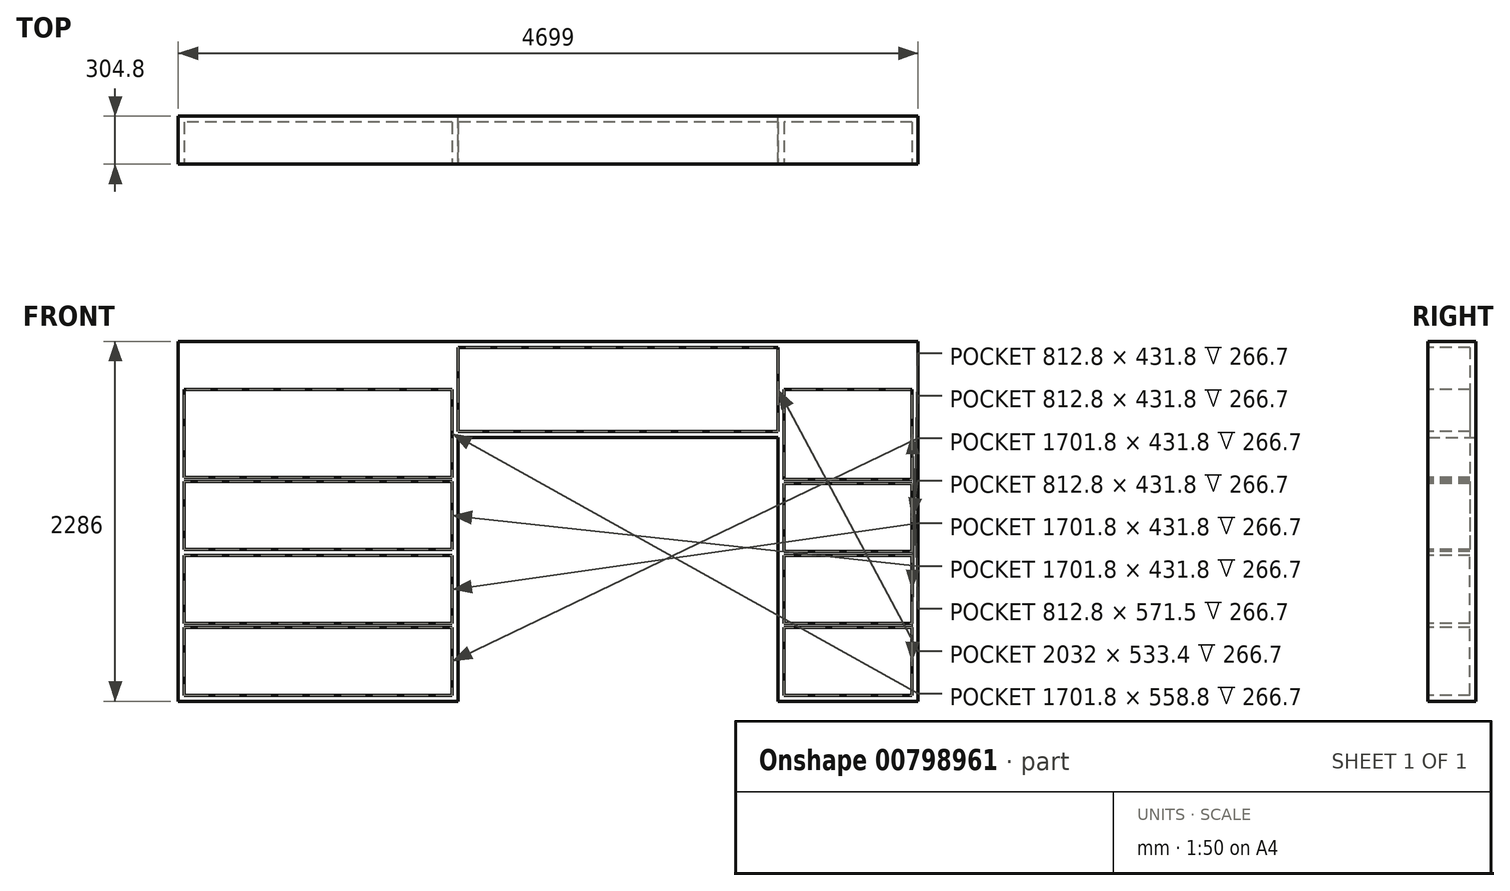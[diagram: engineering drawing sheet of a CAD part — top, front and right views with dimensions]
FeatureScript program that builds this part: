
annotation { "Feature Type Name" : "Feature", "Feature Type Description" : "" }
export const myFeature = defineFeature(function(context is Context, id is Id, definition is map)
    precondition{}
    {
        {
            var Q0;
            Q0=qCreatedBy(makeId("Front.planeOp"),FACE);
            var sketch = newSketch(context, id + "F0", { "sketchPlane" : qUnion([Q0])});
            skLineSegment(sketch, "E0", {"start": v(0, 0) * mm, "end": v(4699, 0) * mm});
            skLineSegment(sketch, "E1", {"start": v(4699, 0) * mm, "end": v(4699, 2286) * mm});
            skLineSegment(sketch, "E2", {"start": v(4699, 2286) * mm, "end": v(0, 2286) * mm});
            skLineSegment(sketch, "E3", {"start": v(0, 2286) * mm, "end": v(0, 0) * mm});
            skSolve(sketch);
        }
        {
            var Q0;
            Q0 = qSketchRegion(id + "F0", true);
            extrude(context, id + "F1", {"entities" : qUnion([Q0]), "depth" : 304.8 * mm, "offsetDistance" : 25.4 * mm});
        }
        {
            var Q0;
            Q0=qCreatedBy(makeId("Front.planeOp"),FACE);
            var sketch = newSketch(context, id + "F2", { "sketchPlane" : qUnion([Q0])});
            skLineSegment(sketch, "E4", {"start": v(1778, 0) * mm, "end": v(1778, 1676.4) * mm});
            skLineSegment(sketch, "E5", {"start": v(1778, 1676.4) * mm, "end": v(3810, 1676.4) * mm});
            skLineSegment(sketch, "E6", {"start": v(3810, 1676.4) * mm, "end": v(3810, 0) * mm});
            skLineSegment(sketch, "E7", {"start": v(3810, 0) * mm, "end": v(1778, 0) * mm});
            skSolve(sketch);
        }
        {
            var Q0;
            Q0 = qSketchRegion(id + "F2", true);
            extrude(context, id + "F3", {"entities" : qUnion([Q0]), "operationType" : NewBodyOperationType.REMOVE, "depth" : 304.8 * mm, "offsetDistance" : 25.4 * mm});
        }
        {
            var Q0;
            Q0=makeQuery(id+"F1.opExtrude","CAP_FACE",FACE,{"disambiguationData":[OSD([sQuery(id+"F0.wireOp",EDGE,"E0"),sQuery(id+"F0.wireOp",EDGE,"E1"),sQuery(id+"F0.wireOp",EDGE,"E2"),sQuery(id+"F0.wireOp",EDGE,"E3")])],"isStart":false});
            var sketch = newSketch(context, id + "F4", { "sketchPlane" : qUnion([Q0])});
            skLineSegment(sketch, "E8", {"start": v(3848.1, 38.1) * mm, "end": v(3848.1, 469.9) * mm});
            skLineSegment(sketch, "E9", {"start": v(3848.1, 469.9) * mm, "end": v(4660.9, 469.9) * mm});
            skLineSegment(sketch, "E10", {"start": v(4660.9, 469.9) * mm, "end": v(4660.9, 38.1) * mm});
            skLineSegment(sketch, "E11", {"start": v(4660.9, 38.1) * mm, "end": v(3848.1, 38.1) * mm});
            skSolve(sketch);
        }
        {
            var Q0;
            Q0 = qSketchRegion(id + "F4", true);
            extrude(context, id + "F5", {"entities" : qUnion([Q0]), "operationType" : NewBodyOperationType.REMOVE, "oppositeDirection" : true, "depth" : 266.7 * mm, "offsetDistance" : 25.4 * mm});
        }
        {
            var Q0;
            Q0=makeQuery(id+"F1.opExtrude","CAP_FACE",FACE,{"disambiguationData":[OSD([sQuery(id+"F0.wireOp",EDGE,"E0"),sQuery(id+"F0.wireOp",EDGE,"E1"),sQuery(id+"F0.wireOp",EDGE,"E2"),sQuery(id+"F0.wireOp",EDGE,"E3")])],"isStart":false});
            var sketch = newSketch(context, id + "F6", { "sketchPlane" : qUnion([Q0])});
            skLineSegment(sketch, "E12", {"start": v(3848.1, 927.1) * mm, "end": v(4660.9, 927.1) * mm});
            skLineSegment(sketch, "E13", {"start": v(4660.9, 927.1) * mm, "end": v(4660.9, 495.3) * mm});
            skLineSegment(sketch, "E14", {"start": v(4660.9, 495.3) * mm, "end": v(3848.1, 495.3) * mm});
            skLineSegment(sketch, "E15", {"start": v(3848.1, 495.3) * mm, "end": v(3848.1, 927.1) * mm});
            skSolve(sketch);
        }
        {
            var Q0;
            Q0 = qSketchRegion(id + "F6", true);
            extrude(context, id + "F7", {"entities" : qUnion([Q0]), "operationType" : NewBodyOperationType.REMOVE, "oppositeDirection" : true, "depth" : 266.7 * mm, "offsetDistance" : 25.4 * mm});
        }
        {
            var Q0;
            Q0=makeQuery(id+"F1.opExtrude","CAP_FACE",FACE,{"disambiguationData":[OSD([sQuery(id+"F0.wireOp",EDGE,"E0"),sQuery(id+"F0.wireOp",EDGE,"E1"),sQuery(id+"F0.wireOp",EDGE,"E2"),sQuery(id+"F0.wireOp",EDGE,"E3")])],"isStart":false});
            var sketch = newSketch(context, id + "F8", { "sketchPlane" : qUnion([Q0])});
            skLineSegment(sketch, "E16", {"start": v(38.1, 469.9) * mm, "end": v(38.1, 38.1) * mm});
            skLineSegment(sketch, "E17", {"start": v(38.1, 38.1) * mm, "end": v(1739.9, 38.1) * mm});
            skLineSegment(sketch, "E18", {"start": v(1739.9, 38.1) * mm, "end": v(1739.9, 469.9) * mm});
            skLineSegment(sketch, "E19", {"start": v(1739.9, 469.9) * mm, "end": v(38.1, 469.9) * mm});
            skSolve(sketch);
        }
        {
            var Q0;
            Q0 = qSketchRegion(id + "F8", true);
            extrude(context, id + "F9", {"entities" : qUnion([Q0]), "operationType" : NewBodyOperationType.REMOVE, "oppositeDirection" : true, "depth" : 266.7 * mm, "offsetDistance" : 25.4 * mm});
        }
        {
            var Q0;
            Q0=makeQuery(id+"F1.opExtrude","CAP_FACE",FACE,{"disambiguationData":[OSD([sQuery(id+"F0.wireOp",EDGE,"E0"),sQuery(id+"F0.wireOp",EDGE,"E1"),sQuery(id+"F0.wireOp",EDGE,"E2"),sQuery(id+"F0.wireOp",EDGE,"E3")])],"isStart":false});
            var sketch = newSketch(context, id + "F10", { "sketchPlane" : qUnion([Q0])});
            skLineSegment(sketch, "E20", {"start": v(3848.1, 1384.3) * mm, "end": v(3848.1, 952.5) * mm});
            skLineSegment(sketch, "E21", {"start": v(3848.1, 952.5) * mm, "end": v(4660.9, 952.5) * mm});
            skLineSegment(sketch, "E22", {"start": v(4660.9, 952.5) * mm, "end": v(4660.9, 1384.3) * mm});
            skLineSegment(sketch, "E23", {"start": v(4660.9, 1384.3) * mm, "end": v(3848.1, 1384.3) * mm});
            skSolve(sketch);
        }
        {
            var Q0;
            Q0 = qSketchRegion(id + "F10", true);
            extrude(context, id + "F11", {"entities" : qUnion([Q0]), "operationType" : NewBodyOperationType.REMOVE, "oppositeDirection" : true, "depth" : 266.7 * mm, "offsetDistance" : 25.4 * mm});
        }
        {
            var Q0;
            Q0=makeQuery(id+"F1.opExtrude","CAP_FACE",FACE,{"disambiguationData":[OSD([sQuery(id+"F0.wireOp",EDGE,"E0"),sQuery(id+"F0.wireOp",EDGE,"E1"),sQuery(id+"F0.wireOp",EDGE,"E2"),sQuery(id+"F0.wireOp",EDGE,"E3")])],"isStart":false});
            var sketch = newSketch(context, id + "F12", { "sketchPlane" : qUnion([Q0])});
            skLineSegment(sketch, "E24", {"start": v(38.1, 927.1) * mm, "end": v(38.1, 495.3) * mm});
            skLineSegment(sketch, "E25", {"start": v(38.1, 495.3) * mm, "end": v(1739.9, 495.3) * mm});
            skLineSegment(sketch, "E26", {"start": v(1739.9, 495.3) * mm, "end": v(1739.9, 927.1) * mm});
            skLineSegment(sketch, "E27", {"start": v(1739.9, 927.1) * mm, "end": v(38.1, 927.1) * mm});
            skSolve(sketch);
        }
        {
            var Q0;
            Q0 = qSketchRegion(id + "F12", true);
            extrude(context, id + "F13", {"entities" : qUnion([Q0]), "operationType" : NewBodyOperationType.REMOVE, "oppositeDirection" : true, "depth" : 266.7 * mm, "offsetDistance" : 25.4 * mm});
        }
        {
            var Q0;
            Q0=makeQuery(id+"F1.opExtrude","CAP_FACE",FACE,{"disambiguationData":[OSD([sQuery(id+"F0.wireOp",EDGE,"E0"),sQuery(id+"F0.wireOp",EDGE,"E1"),sQuery(id+"F0.wireOp",EDGE,"E2"),sQuery(id+"F0.wireOp",EDGE,"E3")])],"isStart":false});
            var sketch = newSketch(context, id + "F14", { "sketchPlane" : qUnion([Q0])});
            skLineSegment(sketch, "E28", {"start": v(38.1, 1397) * mm, "end": v(38.1, 965.2) * mm});
            skLineSegment(sketch, "E29", {"start": v(38.1, 965.2) * mm, "end": v(1739.9, 965.2) * mm});
            skLineSegment(sketch, "E30", {"start": v(1739.9, 965.2) * mm, "end": v(1739.9, 1397) * mm});
            skLineSegment(sketch, "E31", {"start": v(1739.9, 1397) * mm, "end": v(38.1, 1397) * mm});
            skSolve(sketch);
        }
        {
            var Q0;
            Q0 = qSketchRegion(id + "F14", true);
            extrude(context, id + "F15", {"entities" : qUnion([Q0]), "operationType" : NewBodyOperationType.REMOVE, "oppositeDirection" : true, "depth" : 266.7 * mm, "offsetDistance" : 25.4 * mm});
        }
        {
            var Q0;
            Q0=makeQuery(id+"F1.opExtrude","CAP_FACE",FACE,{"disambiguationData":[OSD([sQuery(id+"F0.wireOp",EDGE,"E0"),sQuery(id+"F0.wireOp",EDGE,"E1"),sQuery(id+"F0.wireOp",EDGE,"E2"),sQuery(id+"F0.wireOp",EDGE,"E3")])],"isStart":false});
            var sketch = newSketch(context, id + "F16", { "sketchPlane" : qUnion([Q0])});
            skLineSegment(sketch, "E32", {"start": v(3848.1, 1981.2) * mm, "end": v(3848.1, 1409.7) * mm});
            skLineSegment(sketch, "E33", {"start": v(3848.1, 1409.7) * mm, "end": v(4660.9, 1409.7) * mm});
            skLineSegment(sketch, "E34", {"start": v(4660.9, 1409.7) * mm, "end": v(4660.9, 1981.2) * mm});
            skLineSegment(sketch, "E35", {"start": v(4660.9, 1981.2) * mm, "end": v(3848.1, 1981.2) * mm});
            skSolve(sketch);
        }
        {
            var Q0;
            Q0 = qSketchRegion(id + "F16", true);
            extrude(context, id + "F17", {"entities" : qUnion([Q0]), "operationType" : NewBodyOperationType.REMOVE, "oppositeDirection" : true, "depth" : 266.7 * mm, "offsetDistance" : 25.4 * mm});
        }
        {
            var Q0;
            Q0=makeQuery(id+"F1.opExtrude","CAP_FACE",FACE,{"disambiguationData":[OSD([sQuery(id+"F0.wireOp",EDGE,"E0"),sQuery(id+"F0.wireOp",EDGE,"E1"),sQuery(id+"F0.wireOp",EDGE,"E2"),sQuery(id+"F0.wireOp",EDGE,"E3")])],"isStart":false});
            var sketch = newSketch(context, id + "F18", { "sketchPlane" : qUnion([Q0])});
            skLineSegment(sketch, "E36", {"start": v(1778, 2247.9) * mm, "end": v(1778, 1714.5) * mm});
            skLineSegment(sketch, "E37", {"start": v(1778, 1714.5) * mm, "end": v(3810, 1714.5) * mm});
            skLineSegment(sketch, "E38", {"start": v(3810, 1714.5) * mm, "end": v(3810, 2247.9) * mm});
            skLineSegment(sketch, "E39", {"start": v(3810, 2247.9) * mm, "end": v(1778, 2247.9) * mm});
            skSolve(sketch);
        }
        {
            var Q0;
            Q0 = qSketchRegion(id + "F18", true);
            extrude(context, id + "F19", {"entities" : qUnion([Q0]), "operationType" : NewBodyOperationType.REMOVE, "oppositeDirection" : true, "depth" : 266.7 * mm, "offsetDistance" : 25.4 * mm});
        }
        {
            var Q0;
            Q0=makeQuery(id+"F1.opExtrude","CAP_FACE",FACE,{"disambiguationData":[OSD([sQuery(id+"F0.wireOp",EDGE,"E0"),sQuery(id+"F0.wireOp",EDGE,"E1"),sQuery(id+"F0.wireOp",EDGE,"E2"),sQuery(id+"F0.wireOp",EDGE,"E3")])],"isStart":false});
            var sketch = newSketch(context, id + "F20", { "sketchPlane" : qUnion([Q0])});
            skLineSegment(sketch, "E40", {"start": v(38.1, 1981.2) * mm, "end": v(38.1, 1422.4) * mm});
            skLineSegment(sketch, "E41", {"start": v(38.1, 1422.4) * mm, "end": v(1739.9, 1422.4) * mm});
            skLineSegment(sketch, "E42", {"start": v(1739.9, 1422.4) * mm, "end": v(1739.9, 1981.2) * mm});
            skPoint(sketch, "E42.endSnap0", {"position": v(1778, 1981.2) * mm});
            skLineSegment(sketch, "E43", {"start": v(1739.9, 1981.2) * mm, "end": v(38.1, 1981.2) * mm});
            skSolve(sketch);
        }
        {
            var Q0;
            Q0 = qSketchRegion(id + "F20", true);
            extrude(context, id + "F21", {"entities" : qUnion([Q0]), "operationType" : NewBodyOperationType.REMOVE, "oppositeDirection" : true, "depth" : 266.7 * mm, "offsetDistance" : 25.4 * mm});
        }
    });
